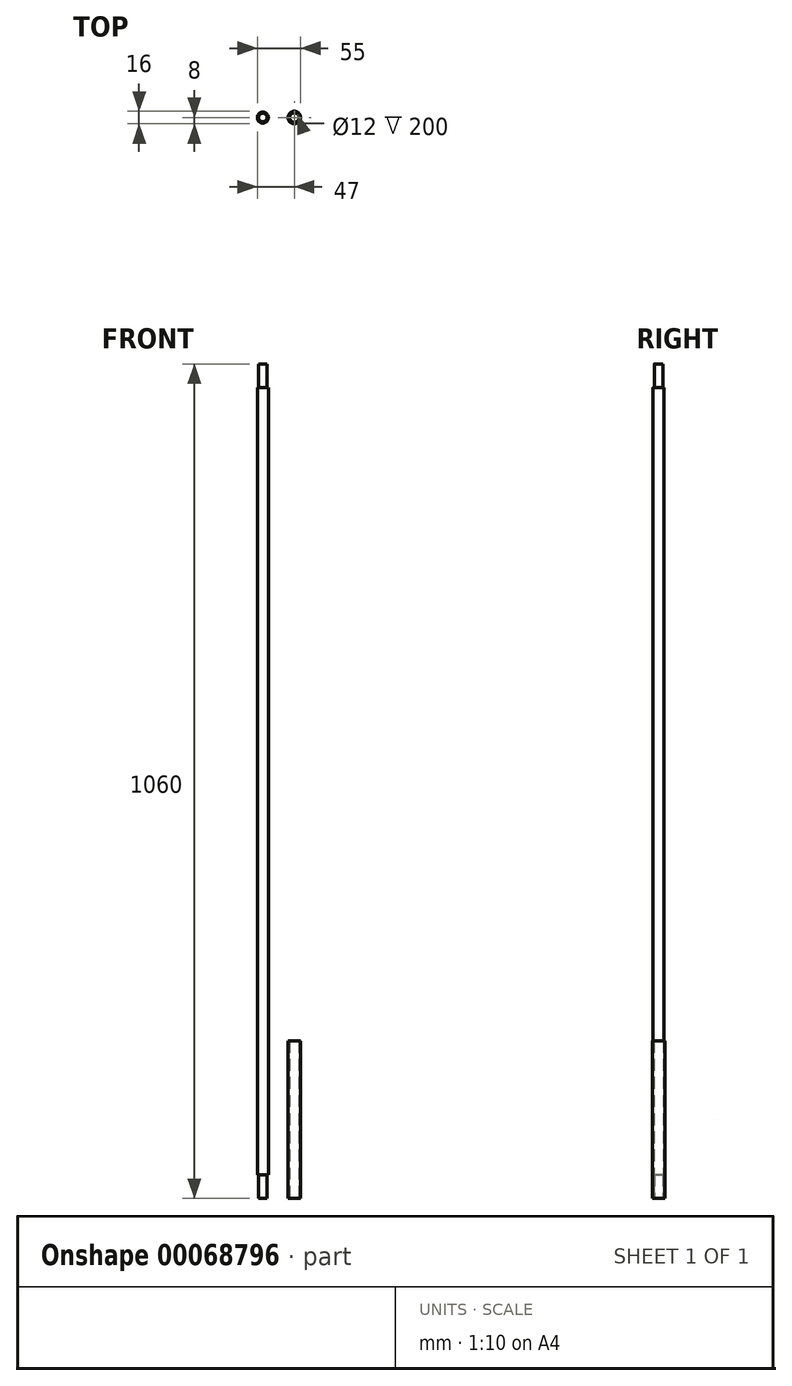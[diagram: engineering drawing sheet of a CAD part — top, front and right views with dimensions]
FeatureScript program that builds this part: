
annotation { "Feature Type Name" : "Feature", "Feature Type Description" : "" }
export const myFeature = defineFeature(function(context is Context, id is Id, definition is map)
    precondition{}
    {
        {
            assignVariable(context, id + "F0", {"name" : "length", "anyValue" : 1000});
        }
        {
            assignVariable(context, id + "F1", {"name" : "threading", "anyValue" : 30});
        }
        {
            assignVariable(context, id + "F2", {"name" : "crosslinklength", "anyValue" : 140});
        }
        {
            var Q0;
            Q0=qCreatedBy(makeId("Top.planeOp"),FACE);
            var sketch = newSketch(context, id + "F3", { "sketchPlane" : qUnion([Q0])});
            skCircle(sketch, "E0", {"center": v(0, 0) * mm, "radius": 7 * mm});
            skCircle(sketch, "E1", {"center": v(0, 0) * mm, "radius": 5.38 * mm});
            skCircle(sketch, "E2", {"center": v(40, 0) * mm, "radius": 6 * mm});
            skCircle(sketch, "E3", {"center": v(40, 0) * mm, "radius": 8 * mm});
            skSolve(sketch);
        }
        {
            var Q0;
            Q0=makeQuery(id+"F3.imprint","IMPRINT",FACE,{"disambiguationData":[TD([[makeQuery(id+"F3.imprint","IMPRINT",EDGE,{"derivedFrom":sQuery(id+"F3.wireOp",EDGE,"E1")}),1.0]])]});
            extrude(context, id + "F4", {"entities" : qUnion([Q0]), "depth" : (getVariable(context, 'length') + 2 * getVariable(context, 'threading')) * mm});
        }
        {
            var Q0;
            Q0=qCreatedBy(makeId("Top.planeOp"),FACE);
            cPlane(context, id + "F5", {"entities" : qUnion([Q0]), "cplaneType" : CPlaneType.OFFSET, "offset" : (getVariable(context, 'threading')) * mm, "width" : 150 * mm, "height" : 150 * mm});
        }
        {
            var Q0;
            Q0=qCreatedBy(id+"F5.planeOp",FACE);
            var sketch = newSketch(context, id + "F6", { "sketchPlane" : qUnion([Q0])});
            skCircle(sketch, "E4.0", {"center": v(0, 0) * mm, "radius": 7 * mm});
            skCircle(sketch, "E5.0", {"center": v(40, 0) * mm, "radius": 8 * mm});
            skSolve(sketch);
        }
        {
            var Q0;
            Q0=makeQuery(id+"F6.imprint","IMPRINT",FACE,{"disambiguationData":[TD([[makeQuery(id+"F6.imprint","IMPRINT",EDGE,{"derivedFrom":sQuery(id+"F6.wireOp",EDGE,"E4.0")}),1.0]])]});
            extrude(context, id + "F7", {"entities" : qUnion([Q0]), "operationType" : NewBodyOperationType.ADD, "depth" : (getVariable(context, 'length')) * mm});
        }
        {
            var Q0;
            Q0=makeQuery(id+"F3.imprint","IMPRINT",FACE,{"disambiguationData":[TD([[makeQuery(id+"F3.imprint","IMPRINT",EDGE,{"derivedFrom":sQuery(id+"F3.wireOp",EDGE,"E2")}),-1.0]])]});
            extrude(context, id + "F8", {"entities" : qUnion([Q0]), "depth" : (getVariable(context, 'crosslinklength') + 2 * getVariable(context, 'threading')) * mm});
        }
    });
